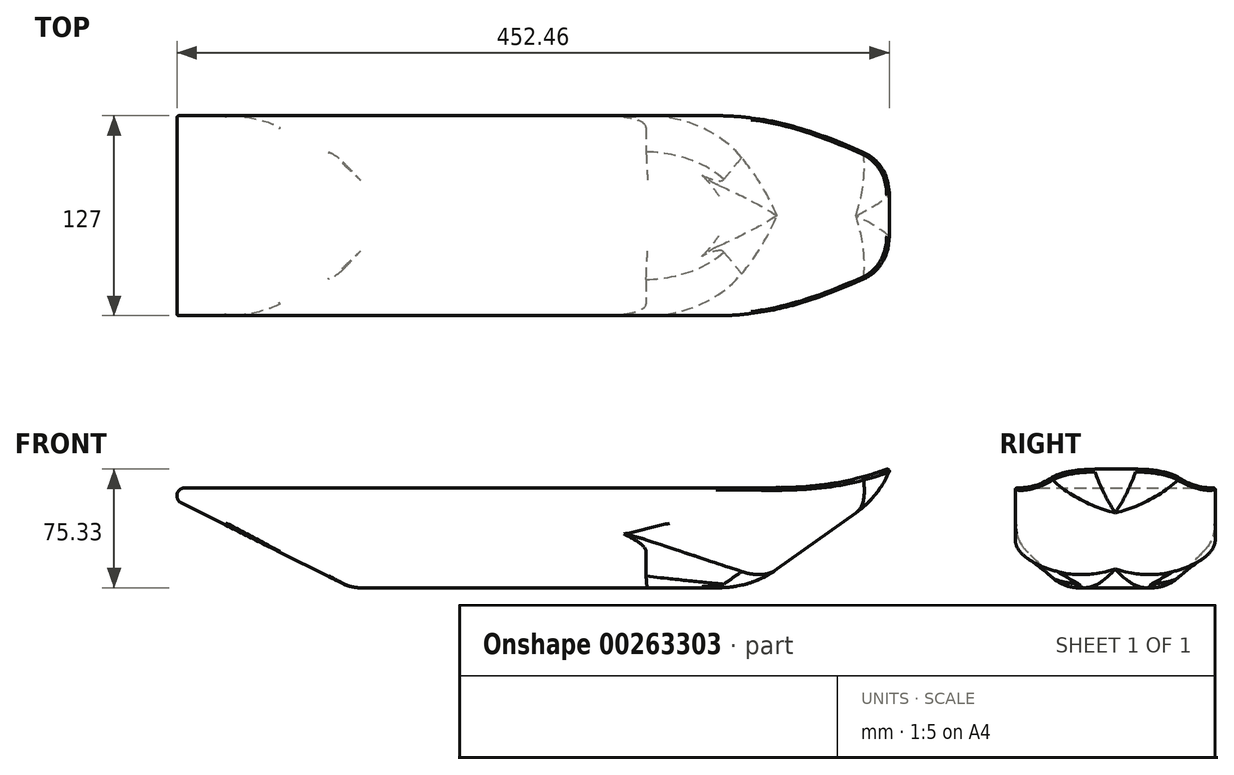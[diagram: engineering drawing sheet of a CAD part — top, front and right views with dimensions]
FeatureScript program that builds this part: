
annotation { "Feature Type Name" : "Feature", "Feature Type Description" : "" }
export const myFeature = defineFeature(function(context is Context, id is Id, definition is map)
    precondition{}
    {
        {
            var Q0;
            Q0=qCreatedBy(makeId("Front.planeOp"),FACE);
            var sketch = newSketch(context, id + "F0", { "sketchPlane" : qUnion([Q0])});
            skLineSegment(sketch, "E0.bottom", {"start": v(-127, 31.75) * mm, "end": v(127, 31.75) * mm});
            skLineSegment(sketch, "E0.top", {"start": v(-127, -31.75) * mm, "end": v(127, -31.75) * mm});
            skLineSegment(sketch, "E0.left", {"start": v(-127, 31.75) * mm, "end": v(-127, -31.75) * mm});
            skLineSegment(sketch, "E0.right", {"start": v(127, 31.75) * mm, "end": v(127, -31.75) * mm});
            skPoint(sketch, "E0.middle", {"position": v(0, 0) * mm});
            skLineSegment(sketch, "E1", {"start": v(127, 31.75) * mm, "end": v(215.9, 31.75) * mm});
            skLineSegment(sketch, "E2", {"start": v(215.9, 31.75) * mm, "end": v(127, -31.75) * mm});
            skLineSegment(sketch, "E3", {"start": v(215.9, 31.75) * mm, "end": v(215.9, 44.45) * mm});
            skFitSpline(sketch, "E4", {"points": [v(127, 31.75) * mm, v(215.9, 44.45) * mm], "startDerivative": vector(97.33, 0) * mm, "endDerivative": vector(107.15, 38.1) * mm});
            skLineSegment(sketch, "E5", {"start": v(-127, 31.75) * mm, "end": v(-232.48, 31.75) * mm});
            skLineSegment(sketch, "E6", {"start": v(-234.75, 22.13) * mm, "end": v(-127, -31.75) * mm});
            skPoint(sketch, "E7.visualSharp", {"position": v(-254, 31.75) * mm});
            skArc(sketch, "E7.filletArc", {"start": v(-232.48, 31.75) * mm, "mid": v(-237.42, 27.84) * mm, "end": v(-234.75, 22.13) * mm});
            skSolve(sketch);
        }
        {
            var Q0;
            Q0=makeQuery(id+"F0.imprint","IMPRINT",FACE,{"disambiguationData":[TD([[makeQuery(id+"F0.imprint","IMPRINT",EDGE,{"derivedFrom":sQuery(id+"F0.wireOp",EDGE,"E0.bottom")}),-1.0]])]});
            extrude(context, id + "F1", {"entities" : qUnion([Q0]), "endBound" : BoundingType.SYMMETRIC, "depth" : 127 * mm});
        }
        {
            var Q0;
            Q0=makeQuery(id+"F0.imprint","IMPRINT",FACE,{"disambiguationData":[TD([[makeQuery(id+"F0.imprint","IMPRINT",EDGE,{"derivedFrom":sQuery(id+"F0.wireOp",EDGE,"E0.left")}),-1.0]])]});
            var Q1;
            Q1=makeQuery(id+"F0.imprint","IMPRINT",FACE,{"disambiguationData":[TD([[makeQuery(id+"F0.imprint","IMPRINT",EDGE,{"derivedFrom":sQuery(id+"F0.wireOp",EDGE,"E0.right")}),1.0]])]});
            var Q2;
            Q2=makeQuery(id+"F0.imprint","IMPRINT",FACE,{"disambiguationData":[TD([[makeQuery(id+"F0.imprint","IMPRINT",EDGE,{"derivedFrom":sQuery(id+"F0.wireOp",EDGE,"E1")}),1.0]])]});
            extrude(context, id + "F2", {"entities" : qUnion([Q0, Q1, Q2]), "operationType" : NewBodyOperationType.ADD, "endBound" : BoundingType.SYMMETRIC, "depth" : 127 * mm});
        }
        {
            var Q0;
            Q0=makeQuery(id+"F2.opExtrude","CAP_EDGE",EDGE,{"disambiguationData":[OSD([sQuery(id+"F0.wireOp",EDGE,"E2")])],"isStart":false});
            var Q1;
            Q1=makeQuery(id+"F2.opExtrude","CAP_EDGE",EDGE,{"disambiguationData":[OSD([sQuery(id+"F0.wireOp",EDGE,"E2")])],"isStart":true});
            var Q2;
            Q2=makeQuery(id+"F2.opExtrude","SWEPT_EDGE",EDGE,{"disambiguationData":[OSD([sQuery(id+"F0.wireOp",EDGE,"E1"),sQuery(id+"F0.wireOp",EDGE,"E2"),sQuery(id+"F0.wireOp",EDGE,"E3")])]});
            var Q3;
            {var subQ0=sQuery(id+"F0.wireOp",EDGE,"E2");var subQ1=sQuery(id+"F0.wireOp",EDGE,"E0.right");var subQ2=sQuery(id+"F0.wireOp",EDGE,"E0.top");Q3=makeQuery(id+"F2.boolean.opBoolean","MERGE",EDGE,{"derivedFrom":[makeQuery(id+"F1.opExtrude","SWEPT_EDGE",EDGE,{"disambiguationData":[OSD([subQ2,subQ1,subQ0])]}),makeQuery(id+"F2.opExtrude","SWEPT_EDGE",EDGE,{"disambiguationData":[OSD([subQ2,subQ1,subQ0])]})]});}
            fillet(context, id + "F3", {"entities" : qUnion([Q0, Q1, Q2, Q3]), "radius" : 63.5 * mm, "tangentPropagation" : true, "allowEdgeOverflow" : false});
        }
        {
            var Q0;
            Q0=makeQuery(id+"F1.opExtrude","CAP_EDGE",EDGE,{"disambiguationData":[OSD([sQuery(id+"F0.wireOp",EDGE,"E0.top")])],"isStart":false});
            var Q1;
            Q1=makeQuery(id+"F1.opExtrude","CAP_EDGE",EDGE,{"disambiguationData":[OSD([sQuery(id+"F0.wireOp",EDGE,"E0.top")])],"isStart":true});
            chamfer(context, id + "F4", {"entities" : qUnion([Q0, Q1]), "width" : 30.48 * mm, "tangentPropagation" : true});
        }
        {
            var Q0;
            {var subQ0=sQuery(id+"F0.wireOp",EDGE,"E0.right");var subQ1=sQuery(id+"F0.wireOp",EDGE,"E0.left");var subQ2=sQuery(id+"F0.wireOp",EDGE,"E0.top");Q0=makeQuery(id+"F4.opChamfer","BLEND_EDGE",EDGE,{"blendedFrom":[makeQuery(id+"F1.opExtrude","CAP_EDGE",EDGE,{"disambiguationData":[OSD([subQ2])],"isStart":false}),makeQuery(id+"F2.boolean.opBoolean","MERGE",FACE,{"derivedFrom":[makeQuery(id+"F1.opExtrude","CAP_FACE",FACE,{"disambiguationData":[OSD([sQuery(id+"F0.wireOp",EDGE,"E0.bottom"),subQ2,subQ1,subQ0])],"isStart":false}),makeQuery(id+"F2.opExtrude","CAP_FACE",FACE,{"disambiguationData":[OSD([subQ1,sQuery(id+"F0.wireOp",EDGE,"E5"),sQuery(id+"F0.wireOp",EDGE,"E6"),sQuery(id+"F0.wireOp",EDGE,"E7.filletArc")])],"isStart":false}),makeQuery(id+"F2.opExtrude","CAP_FACE",FACE,{"disambiguationData":[OSD([subQ0,sQuery(id+"F0.wireOp",EDGE,"E2"),sQuery(id+"F0.wireOp",EDGE,"E3"),sQuery(id+"F0.wireOp",EDGE,"E4")])],"isStart":false})]})],"blendedInto":[makeQuery(id+"F2.boolean.opBoolean","MERGE",FACE,{"derivedFrom":[makeQuery(id+"F1.opExtrude","CAP_FACE",FACE,{"disambiguationData":[OSD([sQuery(id+"F0.wireOp",EDGE,"E0.bottom"),subQ2,subQ1,subQ0])],"isStart":false}),makeQuery(id+"F2.opExtrude","CAP_FACE",FACE,{"disambiguationData":[OSD([subQ1,sQuery(id+"F0.wireOp",EDGE,"E5"),sQuery(id+"F0.wireOp",EDGE,"E6"),sQuery(id+"F0.wireOp",EDGE,"E7.filletArc")])],"isStart":false}),makeQuery(id+"F2.opExtrude","CAP_FACE",FACE,{"disambiguationData":[OSD([subQ0,sQuery(id+"F0.wireOp",EDGE,"E2"),sQuery(id+"F0.wireOp",EDGE,"E3"),sQuery(id+"F0.wireOp",EDGE,"E4")])],"isStart":false})]})]});}
            var Q1;
            {var subQ0=sQuery(id+"F0.wireOp",EDGE,"E0.right");var subQ1=sQuery(id+"F0.wireOp",EDGE,"E0.left");var subQ2=sQuery(id+"F0.wireOp",EDGE,"E0.top");Q1=makeQuery(id+"F4.opChamfer","BLEND_EDGE",EDGE,{"blendedFrom":[makeQuery(id+"F1.opExtrude","CAP_EDGE",EDGE,{"disambiguationData":[OSD([subQ2])],"isStart":true}),makeQuery(id+"F2.boolean.opBoolean","MERGE",FACE,{"derivedFrom":[makeQuery(id+"F1.opExtrude","CAP_FACE",FACE,{"disambiguationData":[OSD([sQuery(id+"F0.wireOp",EDGE,"E0.bottom"),subQ2,subQ1,subQ0])],"isStart":true}),makeQuery(id+"F2.opExtrude","CAP_FACE",FACE,{"disambiguationData":[OSD([subQ1,sQuery(id+"F0.wireOp",EDGE,"E5"),sQuery(id+"F0.wireOp",EDGE,"E6"),sQuery(id+"F0.wireOp",EDGE,"E7.filletArc")])],"isStart":true}),makeQuery(id+"F2.opExtrude","CAP_FACE",FACE,{"disambiguationData":[OSD([subQ0,sQuery(id+"F0.wireOp",EDGE,"E2"),sQuery(id+"F0.wireOp",EDGE,"E3"),sQuery(id+"F0.wireOp",EDGE,"E4")])],"isStart":true})]})],"blendedInto":[makeQuery(id+"F2.boolean.opBoolean","MERGE",FACE,{"derivedFrom":[makeQuery(id+"F1.opExtrude","CAP_FACE",FACE,{"disambiguationData":[OSD([sQuery(id+"F0.wireOp",EDGE,"E0.bottom"),subQ2,subQ1,subQ0])],"isStart":true}),makeQuery(id+"F2.opExtrude","CAP_FACE",FACE,{"disambiguationData":[OSD([subQ1,sQuery(id+"F0.wireOp",EDGE,"E5"),sQuery(id+"F0.wireOp",EDGE,"E6"),sQuery(id+"F0.wireOp",EDGE,"E7.filletArc")])],"isStart":true}),makeQuery(id+"F2.opExtrude","CAP_FACE",FACE,{"disambiguationData":[OSD([subQ0,sQuery(id+"F0.wireOp",EDGE,"E2"),sQuery(id+"F0.wireOp",EDGE,"E3"),sQuery(id+"F0.wireOp",EDGE,"E4")])],"isStart":true})]})]});}
            var Q2;
            {var subQ0=sQuery(id+"F0.wireOp",EDGE,"E2");var subQ1=sQuery(id+"F0.wireOp",EDGE,"E0.right");var subQ2=sQuery(id+"F0.wireOp",EDGE,"E0.left");Q2=makeQuery(id+"F3.opFillet","BLEND_EDGE",EDGE,{"blendedFrom":[makeQuery(id+"F2.opExtrude","CAP_EDGE",EDGE,{"disambiguationData":[OSD([subQ0])],"isStart":false}),makeQuery(id+"F2.boolean.opBoolean","MERGE",FACE,{"derivedFrom":[makeQuery(id+"F1.opExtrude","CAP_FACE",FACE,{"disambiguationData":[OSD([sQuery(id+"F0.wireOp",EDGE,"E0.bottom"),sQuery(id+"F0.wireOp",EDGE,"E0.top"),subQ2,subQ1])],"isStart":false}),makeQuery(id+"F2.opExtrude","CAP_FACE",FACE,{"disambiguationData":[OSD([subQ2,sQuery(id+"F0.wireOp",EDGE,"E5"),sQuery(id+"F0.wireOp",EDGE,"E6"),sQuery(id+"F0.wireOp",EDGE,"E7.filletArc")])],"isStart":false}),makeQuery(id+"F2.opExtrude","CAP_FACE",FACE,{"disambiguationData":[OSD([subQ1,subQ0,sQuery(id+"F0.wireOp",EDGE,"E3"),sQuery(id+"F0.wireOp",EDGE,"E4")])],"isStart":false})]})],"blendedInto":[makeQuery(id+"F2.boolean.opBoolean","MERGE",FACE,{"derivedFrom":[makeQuery(id+"F1.opExtrude","CAP_FACE",FACE,{"disambiguationData":[OSD([sQuery(id+"F0.wireOp",EDGE,"E0.bottom"),sQuery(id+"F0.wireOp",EDGE,"E0.top"),subQ2,subQ1])],"isStart":false}),makeQuery(id+"F2.opExtrude","CAP_FACE",FACE,{"disambiguationData":[OSD([subQ2,sQuery(id+"F0.wireOp",EDGE,"E5"),sQuery(id+"F0.wireOp",EDGE,"E6"),sQuery(id+"F0.wireOp",EDGE,"E7.filletArc")])],"isStart":false}),makeQuery(id+"F2.opExtrude","CAP_FACE",FACE,{"disambiguationData":[OSD([subQ1,subQ0,sQuery(id+"F0.wireOp",EDGE,"E3"),sQuery(id+"F0.wireOp",EDGE,"E4")])],"isStart":false})]})]});}
            var Q3;
            {var subQ0=sQuery(id+"F0.wireOp",EDGE,"E2");var subQ1=sQuery(id+"F0.wireOp",EDGE,"E0.right");var subQ2=sQuery(id+"F0.wireOp",EDGE,"E0.left");Q3=makeQuery(id+"F3.opFillet","BLEND_EDGE",EDGE,{"blendedFrom":[makeQuery(id+"F2.opExtrude","CAP_EDGE",EDGE,{"disambiguationData":[OSD([subQ0])],"isStart":true}),makeQuery(id+"F2.boolean.opBoolean","MERGE",FACE,{"derivedFrom":[makeQuery(id+"F1.opExtrude","CAP_FACE",FACE,{"disambiguationData":[OSD([sQuery(id+"F0.wireOp",EDGE,"E0.bottom"),sQuery(id+"F0.wireOp",EDGE,"E0.top"),subQ2,subQ1])],"isStart":true}),makeQuery(id+"F2.opExtrude","CAP_FACE",FACE,{"disambiguationData":[OSD([subQ2,sQuery(id+"F0.wireOp",EDGE,"E5"),sQuery(id+"F0.wireOp",EDGE,"E6"),sQuery(id+"F0.wireOp",EDGE,"E7.filletArc")])],"isStart":true}),makeQuery(id+"F2.opExtrude","CAP_FACE",FACE,{"disambiguationData":[OSD([subQ1,subQ0,sQuery(id+"F0.wireOp",EDGE,"E3"),sQuery(id+"F0.wireOp",EDGE,"E4")])],"isStart":true})]})],"blendedInto":[makeQuery(id+"F2.boolean.opBoolean","MERGE",FACE,{"derivedFrom":[makeQuery(id+"F1.opExtrude","CAP_FACE",FACE,{"disambiguationData":[OSD([sQuery(id+"F0.wireOp",EDGE,"E0.bottom"),sQuery(id+"F0.wireOp",EDGE,"E0.top"),subQ2,subQ1])],"isStart":true}),makeQuery(id+"F2.opExtrude","CAP_FACE",FACE,{"disambiguationData":[OSD([subQ2,sQuery(id+"F0.wireOp",EDGE,"E5"),sQuery(id+"F0.wireOp",EDGE,"E6"),sQuery(id+"F0.wireOp",EDGE,"E7.filletArc")])],"isStart":true}),makeQuery(id+"F2.opExtrude","CAP_FACE",FACE,{"disambiguationData":[OSD([subQ1,subQ0,sQuery(id+"F0.wireOp",EDGE,"E3"),sQuery(id+"F0.wireOp",EDGE,"E4")])],"isStart":true})]})]});}
            var Q4;
            Q4=makeQuery(id+"F1.opExtrude","SWEPT_FACE",FACE,{"disambiguationData":[OSD([sQuery(id+"F0.wireOp",EDGE,"E0.top")])]});
            fillet(context, id + "F5", {"entities" : qUnion([Q0, Q1, Q2, Q3, Q4]), "radius" : 25.4 * mm, "tangentPropagation" : true, "allowEdgeOverflow" : false});
        }
        {
            var Q0;
            {var subQ0=sQuery(id+"F0.wireOp",EDGE,"E2");Q0=makeQuery(id+"F3.opFillet","BLEND_EDGE",EDGE,{"blendedFrom":[makeQuery(id+"F2.opExtrude","SWEPT_EDGE",EDGE,{"disambiguationData":[OSD([sQuery(id+"F0.wireOp",EDGE,"E1"),subQ0,sQuery(id+"F0.wireOp",EDGE,"E3")])]}),makeQuery(id+"F2.opExtrude","CAP_EDGE",EDGE,{"disambiguationData":[OSD([subQ0])],"isStart":true})],"blendedInto":[]});}
            var Q1;
            {var subQ0=sQuery(id+"F0.wireOp",EDGE,"E2");Q1=makeQuery(id+"F3.opFillet","BLEND_EDGE",EDGE,{"blendedFrom":[makeQuery(id+"F2.opExtrude","SWEPT_EDGE",EDGE,{"disambiguationData":[OSD([sQuery(id+"F0.wireOp",EDGE,"E1"),subQ0,sQuery(id+"F0.wireOp",EDGE,"E3")])]}),makeQuery(id+"F2.opExtrude","CAP_EDGE",EDGE,{"disambiguationData":[OSD([subQ0])],"isStart":false})],"blendedInto":[]});}
            fillet(context, id + "F6", {"entities" : qUnion([Q0, Q1]), "radius" : 38.1 * mm, "tangentPropagation" : true, "allowEdgeOverflow" : false});
        }
        {
            var Q0;
            Q0=makeQuery(id+"F2.boolean.opBoolean","MERGE",EDGE,{"derivedFrom":[makeQuery(id+"F1.opExtrude","CAP_EDGE",EDGE,{"disambiguationData":[OSD([sQuery(id+"F0.wireOp",EDGE,"E0.bottom")])],"isStart":false}),makeQuery(id+"F2.opExtrude","CAP_EDGE",EDGE,{"disambiguationData":[OSD([sQuery(id+"F0.wireOp",EDGE,"E5")])],"isStart":false})]});
            var Q1;
            Q1=makeQuery(id+"F2.boolean.opBoolean","MERGE",EDGE,{"derivedFrom":[makeQuery(id+"F1.opExtrude","CAP_EDGE",EDGE,{"disambiguationData":[OSD([sQuery(id+"F0.wireOp",EDGE,"E0.bottom")])],"isStart":true}),makeQuery(id+"F2.opExtrude","CAP_EDGE",EDGE,{"disambiguationData":[OSD([sQuery(id+"F0.wireOp",EDGE,"E5")])],"isStart":true})]});
            fillet(context, id + "F7", {"entities" : qUnion([Q0, Q1]), "radius" : 1.27 * mm, "tangentPropagation" : true, "allowEdgeOverflow" : false});
        }
    });
